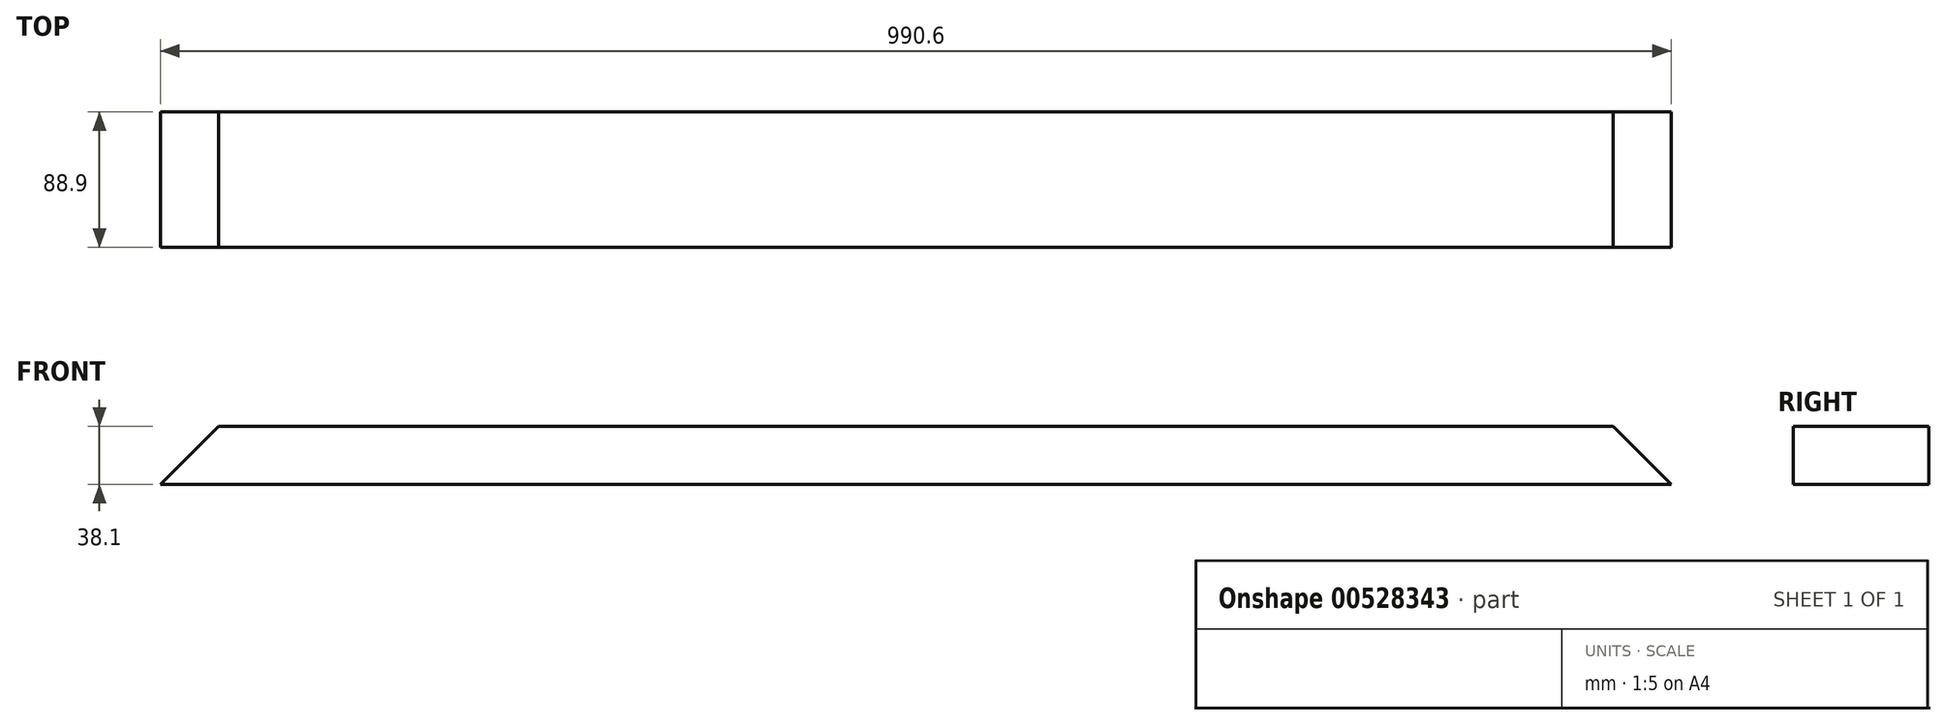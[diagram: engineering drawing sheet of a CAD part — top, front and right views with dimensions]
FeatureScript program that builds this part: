
annotation { "Feature Type Name" : "Feature", "Feature Type Description" : "" }
export const myFeature = defineFeature(function(context is Context, id is Id, definition is map)
    precondition{}
    {
        {
            var Q0;
            Q0=qCreatedBy(makeId("Front.planeOp"),FACE);
            var sketch = newSketch(context, id + "F0", { "sketchPlane" : qUnion([Q0])});
            skLineSegment(sketch, "E0", {"start": v(0, 0) * mm, "end": v(38.1, 38.1) * mm});
            skLineSegment(sketch, "E1", {"start": v(38.1, 38.1) * mm, "end": v(495.3, 38.1) * mm});
            skLineSegment(sketch, "E2", {"start": v(952.5, 38.1) * mm, "end": v(990.6, 0) * mm});
            skLineSegment(sketch, "E3", {"start": v(990.6, 0) * mm, "end": v(0, 0) * mm});
            skPoint(sketch, "E4.end.orphan", {"position": v(495.3, 0) * mm});
            skPoint(sketch, "E4.start.orphan", {"position": v(495.3, 38.1) * mm});
            skLineSegment(sketch, "E5", {"start": v(495.3, 38.1) * mm, "end": v(952.5, 38.1) * mm});
            skSolve(sketch);
        }
        {
            var Q0;
            Q0 = qSketchRegion(id + "F0", true);
            extrude(context, id + "F1", {"entities" : qUnion([Q0]), "oppositeDirection" : true, "depth" : 88.9 * mm, "offsetDistance" : 25.4 * mm});
        }
    });
